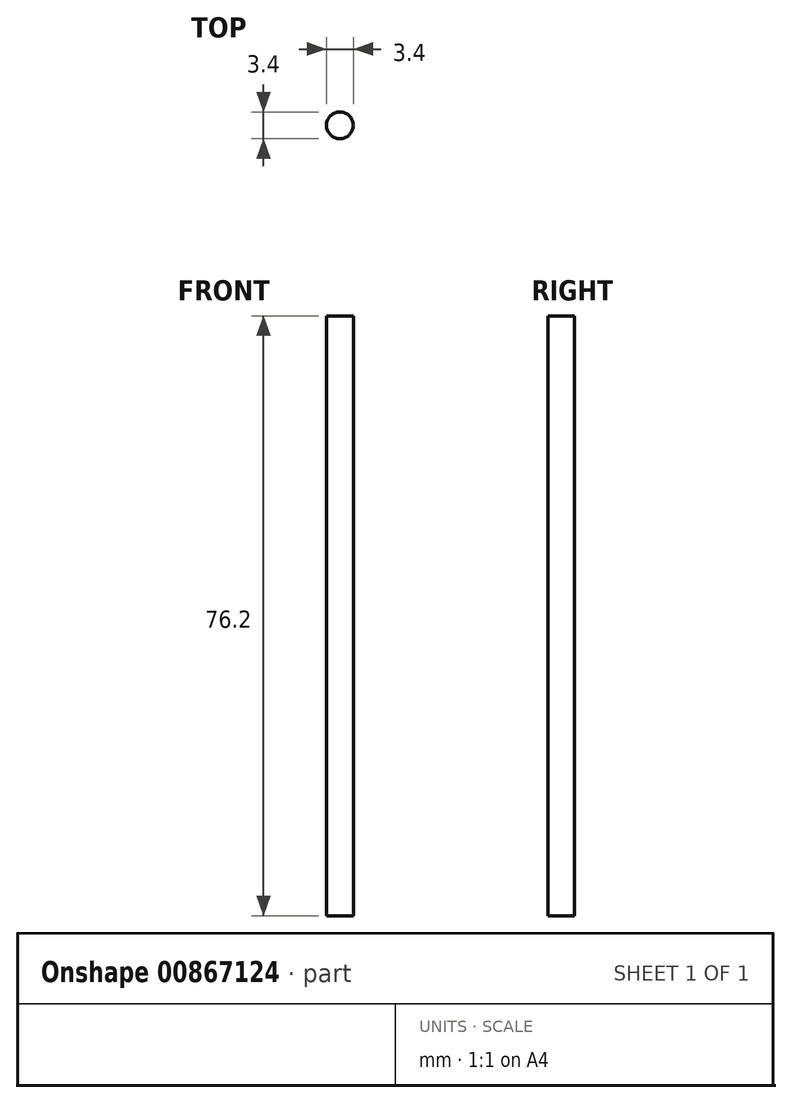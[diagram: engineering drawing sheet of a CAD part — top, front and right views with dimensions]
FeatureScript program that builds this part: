
annotation { "Feature Type Name" : "Feature", "Feature Type Description" : "" }
export const myFeature = defineFeature(function(context is Context, id is Id, definition is map)
    precondition{}
    {
        {
            var Q0;
            Q0=qCreatedBy(makeId("Top.planeOp"),FACE);
            var sketch = newSketch(context, id + "F0", { "sketchPlane" : qUnion([Q0])});
            skCircle(sketch, "E0", {"center": v(0, 0) * mm, "radius": 1.7 * mm});
            skSolve(sketch);
        }
        {
            var Q0;
            Q0=makeQuery(id+"F0.imprint","IMPRINT",FACE,{"disambiguationData":[TD([[makeQuery(id+"F0.imprint","IMPRINT",EDGE,{"derivedFrom":sQuery(id+"F0.wireOp",EDGE,"E0")}),1.0]])]});
            extrude(context, id + "F1", {"entities" : qUnion([Q0]), "depth" : 76.2 * mm, "offsetDistance" : 25.4 * mm});
        }
    });
